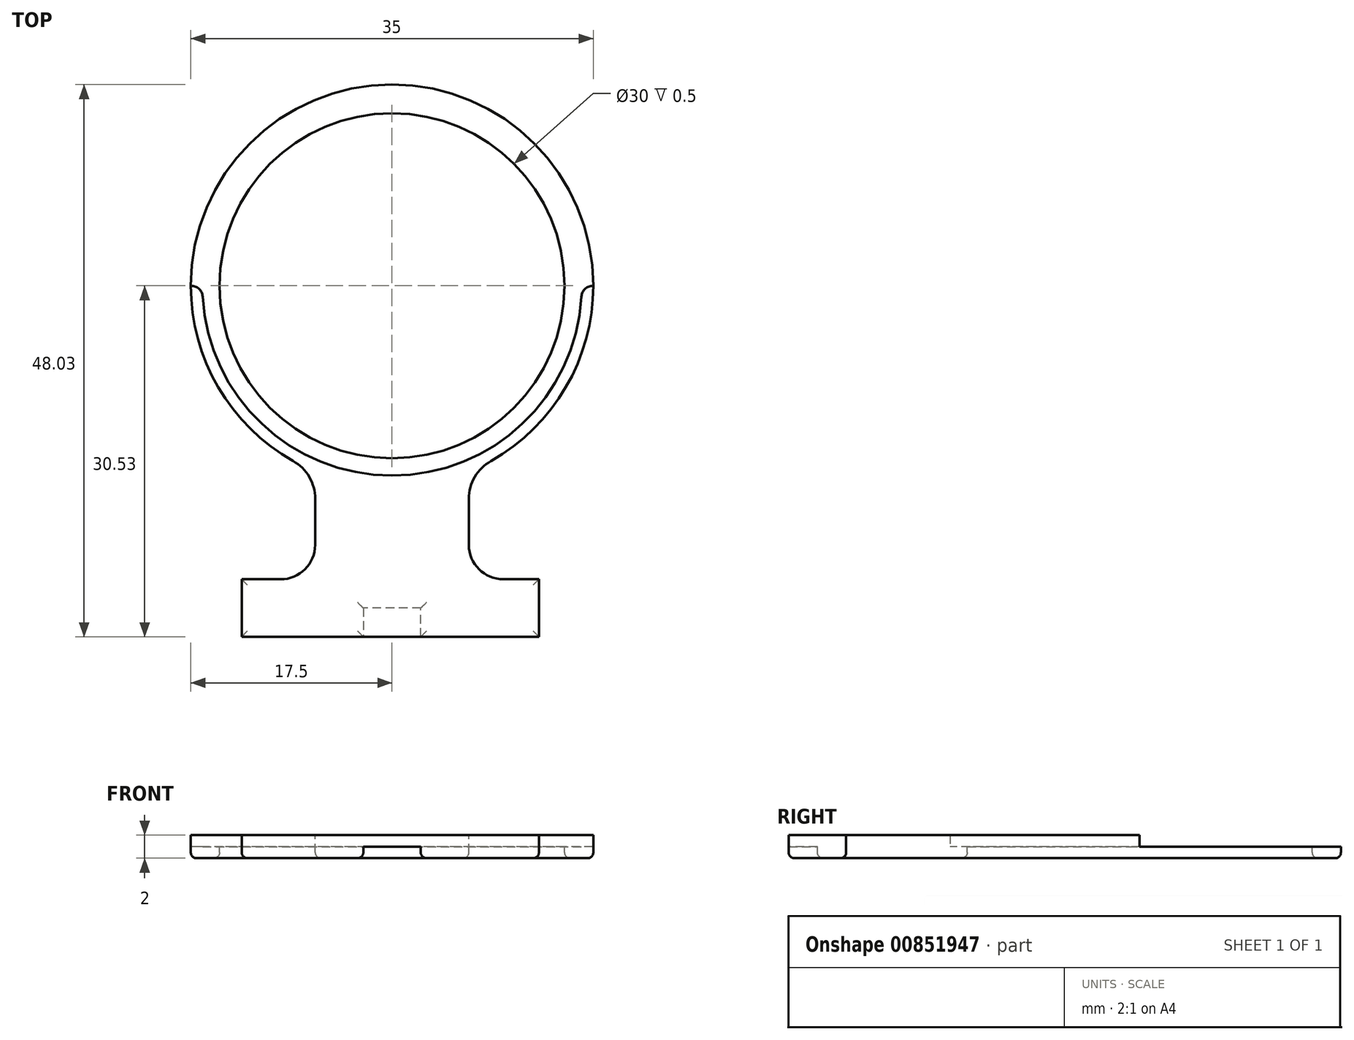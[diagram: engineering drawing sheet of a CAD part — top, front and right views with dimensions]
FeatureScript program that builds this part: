
annotation { "Feature Type Name" : "Feature", "Feature Type Description" : "" }
export const myFeature = defineFeature(function(context is Context, id is Id, definition is map)
    precondition{}
    {
        {
            var Q0;
            Q0=qCreatedBy(makeId("Top.planeOp"),FACE);
            var sketch = newSketch(context, id + "F0", { "sketchPlane" : qUnion([Q0])});
            skCircle(sketch, "E0", {"center": v(0, 0) * mm, "radius": 17.5 * mm});
            skCircle(sketch, "E1", {"center": v(0, 0) * mm, "radius": 15 * mm});
            skLineSegment(sketch, "E2", {"start": v(9.68, -25.52) * mm, "end": v(12.78, -25.52) * mm});
            skLineSegment(sketch, "E3", {"start": v(-9.69, -25.53) * mm, "end": v(-13.07, -25.53) * mm});
            skLineSegment(sketch, "E4", {"start": v(12.78, -25.52) * mm, "end": v(12.78, -30.52) * mm});
            skLineSegment(sketch, "E5", {"start": v(-13.07, -25.53) * mm, "end": v(-13.07, -30.53) * mm});
            skLineSegment(sketch, "E6", {"start": v(2.5, -30.52) * mm, "end": v(2.5, -28.02) * mm});
            skLineSegment(sketch, "E7", {"start": v(2.5, -28.02) * mm, "end": v(-2.5, -28.02) * mm});
            skLineSegment(sketch, "E8", {"start": v(-2.5, -28.02) * mm, "end": v(-2.5, -30.53) * mm});
            skLineSegment(sketch, "E9", {"start": v(12.78, -30.52) * mm, "end": v(2.5, -30.52) * mm});
            skLineSegment(sketch, "E10", {"start": v(-2.5, -30.53) * mm, "end": v(-13.07, -30.53) * mm});
            skLineSegment(sketch, "E11", {"start": v(6.68, -22.52) * mm, "end": v(6.68, -18.52) * mm});
            skLineSegment(sketch, "E12", {"start": v(-6.69, -22.53) * mm, "end": v(-6.69, -18.53) * mm});
            skPoint(sketch, "E13.newPointB", {"position": v(6.68, -25.52) * mm});
            skArc(sketch, "E13.filletArc", {"start": v(6.68, -22.52) * mm, "mid": v(7.56, -24.65) * mm, "end": v(9.68, -25.52) * mm});
            skPoint(sketch, "E14.newPointB", {"position": v(-6.69, -25.53) * mm});
            skArc(sketch, "E14.filletArc", {"start": v(-9.69, -25.53) * mm, "mid": v(-7.56, -24.65) * mm, "end": v(-6.69, -22.53) * mm});
            skArc(sketch, "E15", {"start": v(6.68, -18.52) * mm, "mid": v(7.2, -16.62) * mm, "end": v(8.6, -15.24) * mm});
            skArc(sketch, "E16", {"start": v(-6.69, -18.53) * mm, "mid": v(-7.2, -16.62) * mm, "end": v(-8.6, -15.24) * mm});
            skCircle(sketch, "E17", {"center": v(3.2, -20) * mm, "radius": 2 * mm});
            skLineSegment(sketch, "E18.0", {"start": v(-3.2, -22) * mm, "end": v(-4.6, -21.41) * mm});
            skLineSegment(sketch, "E18.1", {"start": v(-4.6, -21.41) * mm, "end": v(-5.2, -20) * mm});
            skLineSegment(sketch, "E18.2", {"start": v(-5.2, -20) * mm, "end": v(-4.6, -18.59) * mm});
            skLineSegment(sketch, "E18.3", {"start": v(-4.6, -18.59) * mm, "end": v(-3.2, -18) * mm});
            skLineSegment(sketch, "E18.4", {"start": v(-3.2, -18) * mm, "end": v(-1.78, -18.59) * mm});
            skLineSegment(sketch, "E18.5", {"start": v(-1.78, -18.59) * mm, "end": v(-1.2, -20) * mm});
            skLineSegment(sketch, "E18.6", {"start": v(-1.2, -20) * mm, "end": v(-1.78, -21.41) * mm});
            skLineSegment(sketch, "E18.7", {"start": v(-1.78, -21.41) * mm, "end": v(-3.2, -22) * mm});
            skCircle(sketch, "E19", {"center": v(0, 0) * mm, "radius": 16.5 * mm});
            skLineSegment(sketch, "E20", {"start": v(17.5, 0) * mm, "end": v(16.5, 0) * mm});
            skLineSegment(sketch, "E21", {"start": v(-16.5, 0) * mm, "end": v(-17.5, 0) * mm});
            skSolve(sketch);
        }
        {
            var Q0;
            Q0=qCreatedBy(makeId("Top.planeOp"),FACE);
            cPlane(context, id + "F1", {"entities" : qUnion([Q0]), "cplaneType" : CPlaneType.OFFSET, "offset" : 0 * mm, "width" : 150 * mm, "height" : 150 * mm});
        }
        {
            var Q0;
            Q0=qCreatedBy(id+"F1.planeOp",FACE);
            var sketch = newSketch(context, id + "F2", { "sketchPlane" : qUnion([Q0])});
            skLineSegment(sketch, "E22", {"start": v(9.68, -25.52) * mm, "end": v(12.78, -25.52) * mm});
            skLineSegment(sketch, "E23", {"start": v(-9.69, -25.53) * mm, "end": v(-13.07, -25.53) * mm});
            skLineSegment(sketch, "E24", {"start": v(12.78, -25.52) * mm, "end": v(12.78, -30.52) * mm});
            skLineSegment(sketch, "E25", {"start": v(-13.07, -25.53) * mm, "end": v(-13.07, -30.53) * mm});
            skLineSegment(sketch, "E26", {"start": v(12.78, -30.52) * mm, "end": v(2.5, -30.52) * mm});
            skLineSegment(sketch, "E27", {"start": v(-2.5, -30.52) * mm, "end": v(-13.07, -30.53) * mm});
            skLineSegment(sketch, "E28", {"start": v(6.68, -22.52) * mm, "end": v(6.68, -18.54) * mm});
            skLineSegment(sketch, "E29", {"start": v(-6.69, -22.53) * mm, "end": v(-6.69, -18.53) * mm});
            skPoint(sketch, "E30.newPointB", {"position": v(6.68, -25.54) * mm});
            skArc(sketch, "E30.filletArc", {"start": v(6.68, -22.52) * mm, "mid": v(7.56, -24.65) * mm, "end": v(9.68, -25.52) * mm});
            skPoint(sketch, "E31.newPointB", {"position": v(-6.69, -25.53) * mm});
            skArc(sketch, "E31.filletArc", {"start": v(-9.69, -25.53) * mm, "mid": v(-7.56, -24.65) * mm, "end": v(-6.69, -22.53) * mm});
            skArc(sketch, "E32", {"start": v(6.68, -18.54) * mm, "mid": v(7.18, -16.66) * mm, "end": v(8.55, -15.27) * mm});
            skArc(sketch, "E33", {"start": v(-6.69, -18.53) * mm, "mid": v(-7.2, -16.62) * mm, "end": v(-8.6, -15.24) * mm});
            skCircle(sketch, "E34", {"center": v(3.2, -20) * mm, "radius": 2 * mm});
            skLineSegment(sketch, "E35.0", {"start": v(-3.2, -22) * mm, "end": v(-4.6, -21.41) * mm});
            skLineSegment(sketch, "E35.1", {"start": v(-4.6, -21.41) * mm, "end": v(-5.2, -20) * mm});
            skLineSegment(sketch, "E35.2", {"start": v(-5.2, -20) * mm, "end": v(-4.6, -18.59) * mm});
            skLineSegment(sketch, "E35.3", {"start": v(-4.6, -18.59) * mm, "end": v(-3.2, -18) * mm});
            skLineSegment(sketch, "E35.4", {"start": v(-3.2, -18) * mm, "end": v(-1.78, -18.59) * mm});
            skLineSegment(sketch, "E35.5", {"start": v(-1.78, -18.59) * mm, "end": v(-1.2, -20) * mm});
            skLineSegment(sketch, "E35.6", {"start": v(-1.2, -20) * mm, "end": v(-1.78, -21.41) * mm});
            skLineSegment(sketch, "E35.7", {"start": v(-1.78, -21.41) * mm, "end": v(-3.2, -22) * mm});
            skLineSegment(sketch, "E36", {"start": v(17.5, 0) * mm, "end": v(16.5, 0) * mm});
            skLineSegment(sketch, "E37", {"start": v(-16.5, 0) * mm, "end": v(-17.5, 0) * mm});
            skLineSegment(sketch, "E38", {"start": v(-2.5, -30.52) * mm, "end": v(2.5, -30.52) * mm});
            skArc(sketch, "E39", {"start": v(-16.5, 0) * mm, "mid": v(0, -16.5) * mm, "end": v(16.5, 0) * mm});
            skArc(sketch, "E40", {"start": v(-17.5, 0) * mm, "mid": v(-15.11, -8.82) * mm, "end": v(-8.6, -15.24) * mm});
            skArc(sketch, "E41", {"start": v(17.5, 0) * mm, "mid": v(15.1, -8.85) * mm, "end": v(8.55, -15.27) * mm});
            skLineSegment(sketch, "E42", {"start": v(-2.5, -30.52) * mm, "end": v(-2.5, -28.02) * mm});
            skLineSegment(sketch, "E43", {"start": v(-2.5, -28.02) * mm, "end": v(2.5, -28.02) * mm});
            skLineSegment(sketch, "E44", {"start": v(2.5, -28.02) * mm, "end": v(2.5, -30.52) * mm});
            skSolve(sketch);
        }
        {
            var Q0;
            Q0=qCreatedBy(makeId("Top.planeOp"),FACE);
            cPlane(context, id + "F3", {"entities" : qUnion([Q0]), "cplaneType" : CPlaneType.OFFSET, "offset" : 0 * mm, "oppositeDirection" : true, "width" : 150 * mm, "height" : 150 * mm});
        }
        {
            var Q0;
            Q0 = qSketchRegion(id + "F0", true);
            var Q1;
            Q1=makeQuery(id+"F0.imprint","IMPRINT",FACE,{"disambiguationData":[TD([[makeQuery(id+"F0.imprint","IMPRINT",EDGE,{"derivedFrom":sQuery(id+"F0.wireOp",EDGE,"E1")}),-1.0]])]});
            var Q2;
            Q2=makeQuery(id+"F0.imprint","IMPRINT",FACE,{"disambiguationData":[TD([[makeQuery(id+"F0.imprint","IMPRINT",EDGE,{"derivedFrom":sQuery(id+"F0.wireOp",EDGE,"E17")}),1.0]])]});
            var Q3;
            Q3=makeQuery(id+"F0.imprint","IMPRINT",FACE,{"disambiguationData":[TD([[makeQuery(id+"F0.imprint","IMPRINT",EDGE,{"derivedFrom":sQuery(id+"F0.wireOp",EDGE,"E18.0")}),-1.0]])]});
            extrude(context, id + "F4", {"entities" : qUnion([Q0, Q1, Q2, Q3]), "oppositeDirection" : true, "depth" : 1 * mm, "offsetDistance" : 25 * mm});
        }
        {
            var Q0;
            Q0=makeQuery(id+"F2.imprint","IMPRINT",FACE,{"disambiguationData":[TD([[makeQuery(id+"F2.imprint","IMPRINT",EDGE,{"derivedFrom":sQuery(id+"F2.wireOp",EDGE,"E35.0")}),-1.0]])]});
            var Q1;
            Q1=makeQuery(id+"F2.imprint","IMPRINT",FACE,{"disambiguationData":[TD([[makeQuery(id+"F2.imprint","IMPRINT",EDGE,{"derivedFrom":sQuery(id+"F2.wireOp",EDGE,"E34")}),1.0]])]});
            extrude(context, id + "F5", {"entities" : qUnion([Q0, Q1]), "operationType" : NewBodyOperationType.ADD, "depth" : 1 * mm, "offsetDistance" : 25 * mm});
        }
        {
            var Q0;
            Q0=makeQuery(id+"F0.imprint","IMPRINT",FACE,{"disambiguationData":[TD([[makeQuery(id+"F0.imprint","IMPRINT",EDGE,{"derivedFrom":sQuery(id+"F0.wireOp",EDGE,"E2")}),-1.0]])]});
            var Q1;
            {var subQ0=sQuery(id+"F0.wireOp",EDGE,"E20");Q1=makeQuery(id+"F0.imprint","IMPRINT",FACE,{"disambiguationData":[TD([[makeQuery(id+"F0.imprint","IMPRINT",EDGE,{"derivedFrom":subQ0}),1.0]])]});}
            var Q2;
            Q2=makeQuery(id+"F2.imprint","IMPRINT",FACE,{"disambiguationData":[TD([[makeQuery(id+"F2.imprint","IMPRINT",EDGE,{"derivedFrom":sQuery(id+"F2.wireOp",EDGE,"E38")}),1.0]])]});
            extrude(context, id + "F6", {"entities" : qUnion([Q0, Q1, Q2]), "operationType" : NewBodyOperationType.ADD, "depth" : 1 * mm, "offsetDistance" : 25 * mm});
        }
        {
            var Q0;
            Q0=makeQuery(id+"F6.opExtrude","SWEPT_EDGE",EDGE,{"disambiguationData":[OSD([sQuery(id+"F2.wireOp",EDGE,"E37"),sQuery(id+"F2.wireOp",EDGE,"E39")])]});
            var Q1;
            Q1=makeQuery(id+"F6.opExtrude","SWEPT_EDGE",EDGE,{"disambiguationData":[OSD([sQuery(id+"F2.wireOp",EDGE,"E36"),sQuery(id+"F2.wireOp",EDGE,"E39")])]});
            var Q2;
            Q2=makeQuery(id+"F6.opExtrude","SWEPT_EDGE",EDGE,{"disambiguationData":[OSD([sQuery(id+"F0.wireOp",EDGE,"E19"),sQuery(id+"F0.wireOp",EDGE,"E20")])]});
            var Q3;
            Q3=makeQuery(id+"F6.opExtrude","SWEPT_EDGE",EDGE,{"disambiguationData":[OSD([sQuery(id+"F0.wireOp",EDGE,"E19"),sQuery(id+"F0.wireOp",EDGE,"E21")])]});
            fillet(context, id + "F7", {"entities" : qUnion([Q0, Q1, Q2, Q3]), "radius" : 1 * mm, "tangentPropagation" : true, "defaultsChanged" : false, "vertexSettings" : [], "allowEdgeOverflow" : false});
        }
        {
            var Q0;
            Q0=makeQuery(id+"F4.opExtrude","CAP_FACE",FACE,{"disambiguationData":[OSD([sQuery(id+"F0.wireOp",EDGE,"E0"),sQuery(id+"F0.wireOp",EDGE,"E1"),sQuery(id+"F0.wireOp",EDGE,"E2"),sQuery(id+"F0.wireOp",EDGE,"E3"),sQuery(id+"F0.wireOp",EDGE,"E4"),sQuery(id+"F0.wireOp",EDGE,"E5"),sQuery(id+"F0.wireOp",EDGE,"E6"),sQuery(id+"F0.wireOp",EDGE,"E7"),sQuery(id+"F0.wireOp",EDGE,"E8"),sQuery(id+"F0.wireOp",EDGE,"E9"),sQuery(id+"F0.wireOp",EDGE,"E10"),sQuery(id+"F0.wireOp",EDGE,"E11"),sQuery(id+"F0.wireOp",EDGE,"E12"),sQuery(id+"F0.wireOp",EDGE,"E13.filletArc"),sQuery(id+"F0.wireOp",EDGE,"E14.filletArc"),sQuery(id+"F0.wireOp",EDGE,"E15"),sQuery(id+"F0.wireOp",EDGE,"E16")])],"isStart":false});
            fillet(context, id + "F8", {"entities" : qUnion([Q0]), "radius" : .5 * mm, "tangentPropagation" : true, "allowEdgeOverflow" : false});
        }
    });
